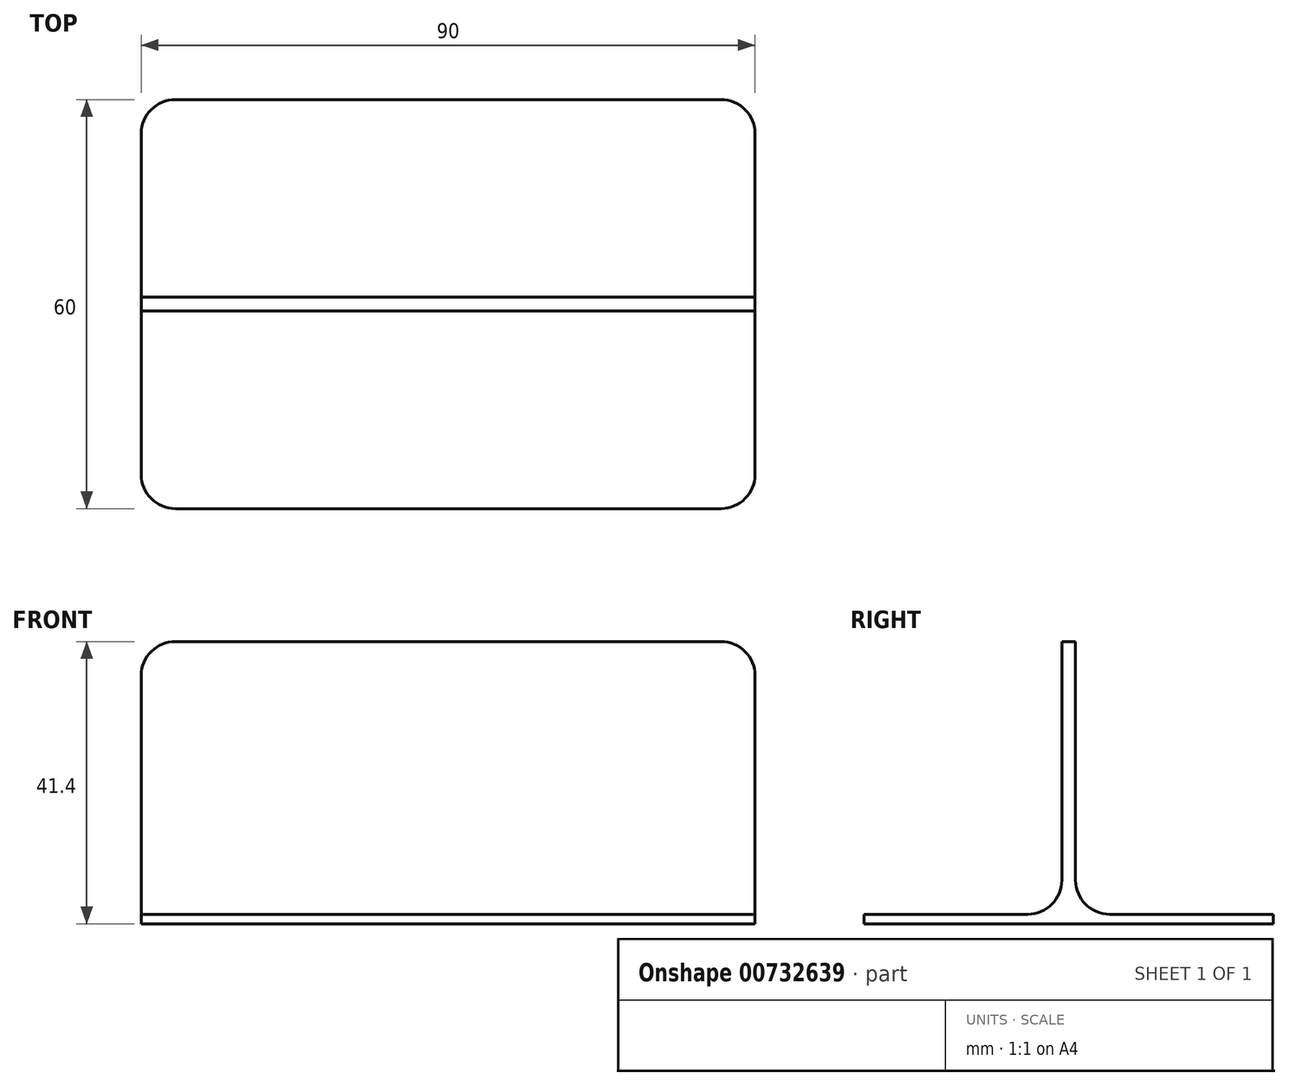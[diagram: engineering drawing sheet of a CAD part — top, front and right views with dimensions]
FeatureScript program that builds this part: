
annotation { "Feature Type Name" : "Feature", "Feature Type Description" : "" }
export const myFeature = defineFeature(function(context is Context, id is Id, definition is map)
    precondition{}
    {
        {
            var Q0;
            Q0=qCreatedBy(makeId("Right.planeOp"),FACE);
            var sketch = newSketch(context, id + "F0", { "sketchPlane" : qUnion([Q0])});
            skLineSegment(sketch, "E0.bottom", {"start": v(30, 0.7) * mm, "end": v(-30, 0.7) * mm});
            skLineSegment(sketch, "E0.top", {"start": v(30, -0.7) * mm, "end": v(-30, -0.7) * mm});
            skLineSegment(sketch, "E0.left", {"start": v(30, 0.7) * mm, "end": v(30, -0.7) * mm});
            skLineSegment(sketch, "E0.right", {"start": v(-30, 0.7) * mm, "end": v(-30, -0.7) * mm});
            skPoint(sketch, "E0.middle", {"position": v(0, 0) * mm});
            skLineSegment(sketch, "E1.bottom", {"start": v(1, 40.7) * mm, "end": v(-1, 40.7) * mm});
            skLineSegment(sketch, "E1.top", {"start": v(1, 0.7) * mm, "end": v(-1, 0.7) * mm});
            skLineSegment(sketch, "E1.left", {"start": v(1, 40.7) * mm, "end": v(1, 0.7) * mm});
            skLineSegment(sketch, "E1.right", {"start": v(-1, 40.7) * mm, "end": v(-1, 0.7) * mm});
            skPoint(sketch, "E1.middle", {"position": v(0, 20.7) * mm});
            skSolve(sketch);
        }
        {
            var Q0;
            Q0=makeQuery(id+"F0.imprint","IMPRINT",FACE,{"disambiguationData":[TD([[makeQuery(id+"F0.imprint","IMPRINT",EDGE,{"derivedFrom":sQuery(id+"F0.wireOp",EDGE,"E1.bottom")}),1.0]])]});
            var Q1;
            Q1=makeQuery(id+"F0.imprint","IMPRINT",FACE,{"disambiguationData":[TD([[makeQuery(id+"F0.imprint","IMPRINT",EDGE,{"derivedFrom":sQuery(id+"F0.wireOp",EDGE,"E0.top")}),-1.0]])]});
            extrude(context, id + "F1", {"entities" : qUnion([Q0, Q1]), "endBound" : BoundingType.SYMMETRIC, "depth" : 90 * mm, "offsetDistance" : 25 * mm});
        }
        {
            var Q0;
            Q0=makeQuery(id+"F1.opExtrude","SWEPT_EDGE",EDGE,{"disambiguationData":[OSD([sQuery(id+"F0.wireOp",EDGE,"E0.bottom"),sQuery(id+"F0.wireOp",EDGE,"E1.right")])]});
            var Q1;
            Q1=makeQuery(id+"F1.opExtrude","SWEPT_EDGE",EDGE,{"disambiguationData":[OSD([sQuery(id+"F0.wireOp",EDGE,"E0.bottom"),sQuery(id+"F0.wireOp",EDGE,"E1.left")])]});
            fillet(context, id + "F2", {"entities" : qUnion([Q0, Q1]), "radius" : 5 * mm, "tangentPropagation" : true, "allowEdgeOverflow" : false});
        }
        {
            var Q0;
            Q0=makeQuery(id+"F1.opExtrude","CAP_EDGE",EDGE,{"disambiguationData":[OSD([sQuery(id+"F0.wireOp",EDGE,"E0.right")])],"isStart":true});
            var Q1;
            Q1=makeQuery(id+"F1.opExtrude","CAP_EDGE",EDGE,{"disambiguationData":[OSD([sQuery(id+"F0.wireOp",EDGE,"E0.left")])],"isStart":true});
            var Q2;
            Q2=makeQuery(id+"F1.opExtrude","CAP_EDGE",EDGE,{"disambiguationData":[OSD([sQuery(id+"F0.wireOp",EDGE,"E0.left")])],"isStart":false});
            var Q3;
            Q3=makeQuery(id+"F1.opExtrude","CAP_EDGE",EDGE,{"disambiguationData":[OSD([sQuery(id+"F0.wireOp",EDGE,"E0.right")])],"isStart":false});
            var Q4;
            Q4=makeQuery(id+"F1.opExtrude","CAP_EDGE",EDGE,{"disambiguationData":[OSD([sQuery(id+"F0.wireOp",EDGE,"E1.bottom")])],"isStart":true});
            var Q5;
            Q5=makeQuery(id+"F1.opExtrude","CAP_EDGE",EDGE,{"disambiguationData":[OSD([sQuery(id+"F0.wireOp",EDGE,"E1.bottom")])],"isStart":false});
            fillet(context, id + "F3", {"entities" : qUnion([Q0, Q1, Q2, Q3, Q4, Q5]), "radius" : 5 * mm, "tangentPropagation" : true, "allowEdgeOverflow" : false});
        }
    });
